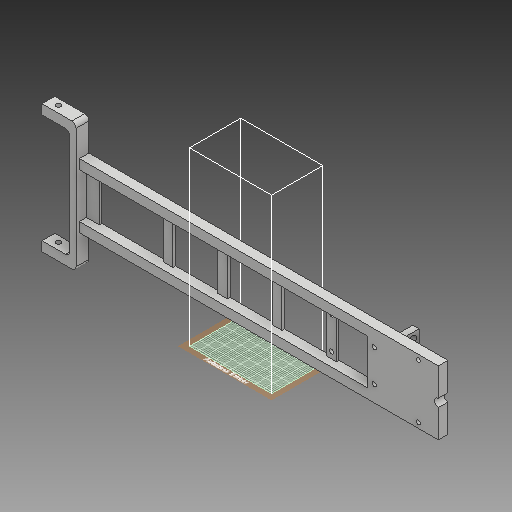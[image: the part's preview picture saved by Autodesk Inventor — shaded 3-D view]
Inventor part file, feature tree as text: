
AUTODESK INVENTOR PART (.ipt)
format: ipt  version: 2018 (Build 220112000, 112)  size: 710,656 bytes
history: native  units: mm
features: sketch x42, extrude x31, fillet x7, hole x6, plane x1
ambient origin geometry x8: Origin, YZ Plane, XZ Plane, XY Plane, X Axis, Y Axis, Z Axis, Center Point
bodies: Solid1 (feature_tree)
feature tree (87):
  extrude  "Extrusion1"  Depth=50.0mm
  hole  "Hole1"  [1 undecoded]
  hole  "Hole2"  [1 undecoded]
  extrude  "Extrusion2"  Depth=25.0mm
  extrude  "Extrusion3"  Depth=25.0mm
  extrude  "Extrusion4"  Depth=5.0mm
  sketch  "Sketch7"  dims[d25=10.0mm d26=5.0mm]
  extrude  "Extrusion5"  Depth=5.0mm
  extrude  "Extrusion6"  Depth=35.0mm
  extrude  "Extrusion7"  Depth=35.0mm
  extrude  "Extrusion8"  Depth=35.0mm
  extrude  "Extrusion9"  Depth=2.0mm TaperAngle=0.0deg
  extrude  "Extrusion10"  Depth=7.5mm TaperAngle=0.0deg
  extrude  "Extrusion11"  Depth=10.0mm
  extrude  "Extrusion12"  Depth=7.5mm
  fillet  "Fillet1"  Radius=7.5mm
  fillet  "Fillet2"  Radius=25.0mm
  fillet  "Fillet3"  Radius=3.0mm
  fillet  "Fillet4"  Radius=3.2mm
  fillet  "Fillet5"  Radius=2.1mm
  fillet  "Fillet6"  Radius=5.5mm
  extrude  "Extrusion13"  Depth=92.5mm TaperAngle=0.0deg
  sketch  "Sketch17"  dims[d58=4.25mm d59=241.0mm d60=0.0mm]
  hole  "Hole3"  [1 undecoded]
  hole  "Hole4"  [1 undecoded]
  extrude  "Extrusion14"  Depth=5.0mm
  extrude  "Extrusion15"  Depth=2.5mm TaperAngle=0.0deg
  extrude  "Extrusion16"  Depth=6.35mm
  extrude  "Extrusion17"  Depth=2.5mm
  extrude  "Extrusion18"  Depth=14.55mm TaperAngle=0.0deg
  extrude  "Extrusion19"  Depth=0.1mm
  extrude  "Extrusion20"  Depth=3.25mm
  extrude  "Extrusion21"  Depth=3.25mm
  hole  "Hole5"  [1 undecoded]
  extrude  "Extrusion22"  Depth=2.0mm
  extrude  "Extrusion23"  Depth=15.0mm
  extrude  "Extrusion24"  Depth=10.0mm TaperAngle=0.0deg
  hole  "Hole6"  [1 undecoded]
  extrude  "Extrusion25"  Depth=100.0mm TaperAngle=0.0deg
  extrude  "Extrusion26"  Depth=2.0mm TaperAngle=0.0deg
  sketch  "Sketch35"  dims[d116=3.3mm d117=3.3mm]
  plane  "Work Plane1"
  sketch  "Sketch36"  dims[d118=3.3mm d119=3.3mm d120=2.0mm d121=0.0mm]
  extrude  "Extrusion27"  Depth=3.3mm
  extrude  "Extrusion28"  Depth=2.0mm
  fillet  "Fillet7"  Radius=2.0mm
  extrude  "Extrusion29"  Depth=8.0mm
  extrude  "Extrusion30"  Depth=21.0mm
  sketch  "Sketch41"  dims[d137=3.5mm]
  sketch  "Sketch42"  dims[d138=21.0mm d139=3.3mm d140=3.3mm d141=3.3mm d142=10.0mm d143=0.0mm d144=7.5mm d145=0.0mm d146=100.0mm d147=0.0mm d148=5.0mm d149=6.0mm d150=4.0mm d151=2.0mm d152=90.0deg d153=15.0mm d154=0.0mm d155=3.75mm d156=100.0mm d157=0.0mm d158=100.0mm d159=0.0mm d160=-0.698132mm d161=5.0mm d162=5.0mm d163=37.5mm d164=0.0mm d165=1.1mm d166=37.5mm d167=0.0mm d168=0.2mm d169=3.0mm d170=5.5mm d171=0.0mm d172=100.0mm d173=0.0mm d174=56.043mm d175=56.043mm d176=74.0mm d177=3.0mm d178=74.0mm d179=3.0mm d180=74.0mm d181=3.0mm d182=74.0mm d183=3.0mm d184=2.0mm d185=0.0mm]
  extrude  "Extrusion31"  Depth=15.825mm
  sketch  "Sketch1"  dims[d0=50.0mm d1=50.0mm]
  sketch  "Sketch2"  dims[d2=240.0mm d3=7.5mm]
  sketch  "Sketch3"  dims[d4=7.5mm d5=7.5mm d6=0.0mm]
  sketch  "Sketch4"  dims[d7=6.35mm d8=6.0mm d9=4.0mm d10=2.0mm d11=90.0deg d12=8.0mm d13=20.594885mm d14=25.0mm]
  sketch  "Sketch5"  dims[d15=3.3mm d16=6.0mm d17=4.0mm d18=2.0mm d19=90.0deg d20=8.0mm d21=20.594885mm d22=25.0mm]
  sketch  "Sketch6"  dims[d23=180.0deg d24=5.0mm]
  sketch  "Sketch8"  dims[d27=17.5mm d28=0.0mm d30=35.0mm]
  sketch  "Sketch9"  dims[d31=35.0mm d32=35.0mm]
  sketch  "Sketch10"  dims[d33=35.0mm d34=35.0mm]
  sketch  "Sketch11"  dims[d35=35.0mm d36=2.0mm d37=0.0mm]
  sketch  "Sketch12"  dims[d38=10.0mm d39=7.5mm d40=0.0mm]
  sketch  "Sketch13"  dims[d41=100.0mm d42=10.0mm]
  sketch  "Sketch14"  dims[d43=7.5mm d44=0.0mm d45=7.5mm d46=7.5mm d47=25.0mm d48=0.0mm d49=3.0mm d50=3.2mm d51=2.1mm d52=5.5mm]
  sketch  "Sketch15"  dims[d53=3.3mm d54=92.5mm d55=0.0mm]
  sketch  "Sketch16"  dims[d56=5.5mm d57=3.3mm]
  sketch  "Sketch18"  dims[d61=4.44mm d62=5.0mm]
  sketch  "Sketch19"  dims[d63=2.5mm d64=91.25mm d65=0.0mm]
  sketch  "Sketch20"  dims[d66=30.0mm d67=6.35mm]
  sketch  "Sketch21"  dims[d68=3.8mm d69=0.0mm d70=2.5mm]
  sketch  "Sketch22"  dims[d71=14.55mm d72=0.0mm d73=14.55mm d74=0.0mm]
  sketch  "Sketch23"  dims[d75=0.1mm d76=0.1mm]
  sketch  "Sketch24"  dims[d77=3.25mm d78=3.25mm]
  sketch  "Sketch25"  dims[d79=3.25mm d80=3.25mm]
  sketch  "Sketch26"  dims[d81=35.0mm d82=10.0mm]
  sketch  "Sketch27"  dims[d83=2.0mm d84=0.0mm d85=3.6mm]
  sketch  "Sketch28"  dims[d86=3.6mm]
  sketch  "Sketch29"  dims[d87=3.3mm d88=6.0mm d89=4.0mm d90=2.0mm d91=90.0deg d92=15.0mm d93=20.594885mm]
  sketch  "Sketch30"  dims[d94=3.3mm d95=6.0mm d96=4.0mm d97=2.0mm d98=90.0deg d99=15.0mm d100=20.594885mm d101=6.0mm]
  sketch  "Sketch31"  dims[d102=20.0mm d103=0.0mm d104=10.0mm d105=0.0mm]
  sketch  "Sketch32"  dims[d106=2.0mm d107=0.0mm d108=4.0mm]
  sketch  "Sketch33"  dims[d109=100.0mm d110=0.0mm d111=100.0mm d112=0.0mm]
  sketch  "Sketch34"  dims[d113=5.0mm d114=2.0mm d115=0.0mm]
  sketch  "Sketch37"  dims[d122=5.5mm d123=0.0mm]
  sketch  "Sketch38"  dims[d124=3.3mm d125=6.0mm d126=4.0mm d127=2.0mm d128=90.0deg d129=8.0mm d130=20.594885mm d131=42.0mm]
  sketch  "Sketch39"  dims[d132=17.0mm d133=21.0mm]
  sketch  "Sketch40"  dims[d135=8.5mm d136=15.825mm]
note: 6 required parameter values undecoded (feature->parameter linkage not recoverable at this tier; creation-order binding heuristic only, values carry confidence <= 0.55)
